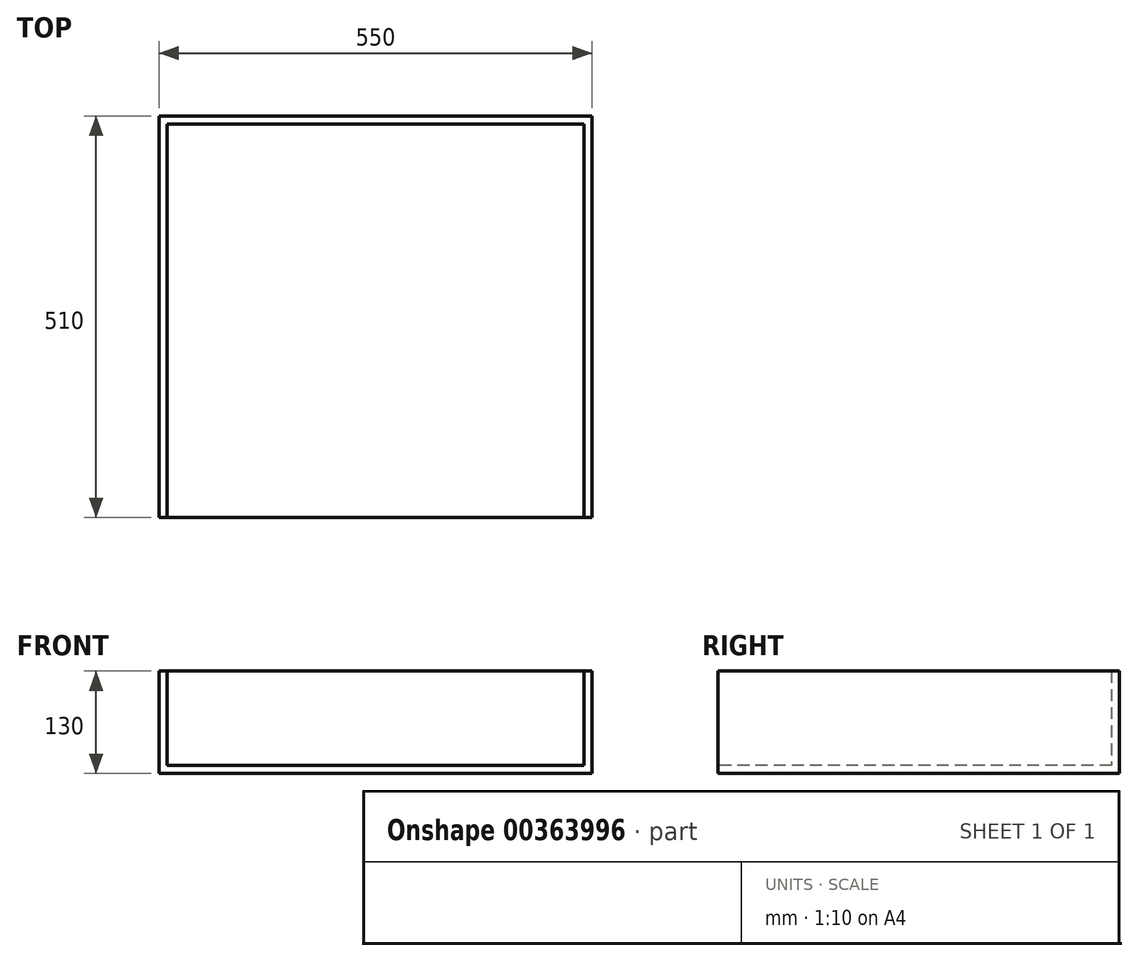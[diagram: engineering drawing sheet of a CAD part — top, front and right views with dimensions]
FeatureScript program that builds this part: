
annotation { "Feature Type Name" : "Feature", "Feature Type Description" : "" }
export const myFeature = defineFeature(function(context is Context, id is Id, definition is map)
    precondition{}
    {
        {
            var Q0;
            Q0=qCreatedBy(makeId("Top.planeOp"),FACE);
            var sketch = newSketch(context, id + "F0", { "sketchPlane" : qUnion([Q0])});
            skLineSegment(sketch, "E0.bottom", {"start": v(275, -255) * mm, "end": v(-275, -255) * mm});
            skLineSegment(sketch, "E0.top", {"start": v(275, 255) * mm, "end": v(-275, 255) * mm});
            skLineSegment(sketch, "E0.left", {"start": v(275, -255) * mm, "end": v(275, 255) * mm});
            skLineSegment(sketch, "E0.right", {"start": v(-275, -255) * mm, "end": v(-275, 255) * mm});
            skPoint(sketch, "E0.middle", {"position": v(0, 0) * mm});
            skSolve(sketch);
        }
        {
            var Q0;
            Q0 = qSketchRegion(id + "F0", true);
            extrude(context, id + "F1", {"entities" : qUnion([Q0]), "depth" : 10 * mm});
        }
        {
            var Q0;
            Q0=makeQuery(id+"F1.opExtrude","CAP_FACE",FACE,{"disambiguationData":[OSD([sQuery(id+"F0.wireOp",EDGE,"E0.bottom"),sQuery(id+"F0.wireOp",EDGE,"E0.top"),sQuery(id+"F0.wireOp",EDGE,"E0.left"),sQuery(id+"F0.wireOp",EDGE,"E0.right")])],"isStart":false});
            var sketch = newSketch(context, id + "F2", { "sketchPlane" : qUnion([Q0])});
            skLineSegment(sketch, "E1", {"start": v(-275, -255) * mm, "end": v(-265, -255) * mm});
            skLineSegment(sketch, "E2", {"start": v(-265, -255) * mm, "end": v(-265, 245) * mm});
            skLineSegment(sketch, "E3", {"start": v(-265, 245) * mm, "end": v(265, 245) * mm});
            skLineSegment(sketch, "E4", {"start": v(265, 245) * mm, "end": v(265, -255) * mm});
            skLineSegment(sketch, "E5", {"start": v(265, -255) * mm, "end": v(275, -255) * mm});
            skLineSegment(sketch, "E6", {"start": v(275, -255) * mm, "end": v(275, 255) * mm});
            skLineSegment(sketch, "E7", {"start": v(275, 255) * mm, "end": v(-275, 255) * mm});
            skLineSegment(sketch, "E8", {"start": v(-275, 255) * mm, "end": v(-275, -255) * mm});
            skLineSegment(sketch, "E9", {"start": v(-265, 245) * mm, "end": v(-265, 255) * mm, "construction": true});
            skSolve(sketch);
        }
        {
            var Q0;
            Q0 = qSketchRegion(id + "F2", true);
            extrude(context, id + "F3", {"entities" : qUnion([Q0]), "operationType" : NewBodyOperationType.ADD, "depth" : 120 * mm});
        }
    });
